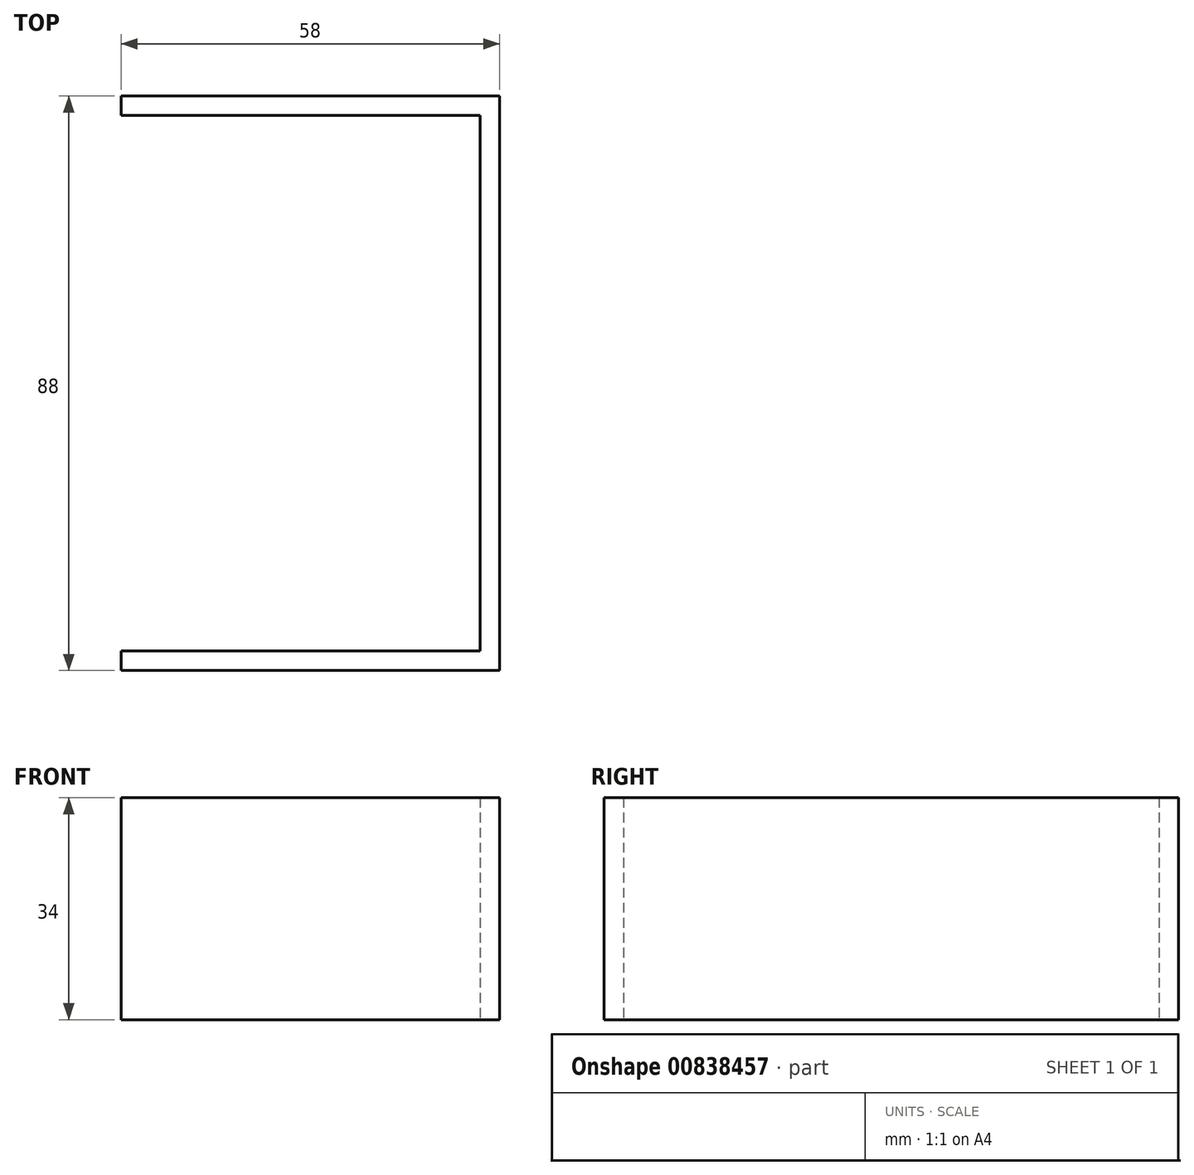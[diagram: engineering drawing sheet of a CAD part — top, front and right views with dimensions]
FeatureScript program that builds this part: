
annotation { "Feature Type Name" : "Feature", "Feature Type Description" : "" }
export const myFeature = defineFeature(function(context is Context, id is Id, definition is map)
    precondition{}
    {
        {
            var Q0;
            Q0=qCreatedBy(makeId("Top.planeOp"),FACE);
            var sketch = newSketch(context, id + "F0", { "sketchPlane" : qUnion([Q0])});
            skLineSegment(sketch, "E0", {"start": v(-18.99, 72.27) * mm, "end": v(39.01, 72.27) * mm});
            skLineSegment(sketch, "E1", {"start": v(39.01, 72.27) * mm, "end": v(39.01, -15.73) * mm});
            skLineSegment(sketch, "E2", {"start": v(39.01, -15.73) * mm, "end": v(-18.99, -15.73) * mm});
            skLineSegment(sketch, "E3", {"start": v(-18.99, -15.73) * mm, "end": v(-18.99, -12.73) * mm});
            skLineSegment(sketch, "E4", {"start": v(-18.99, -12.73) * mm, "end": v(36.01, -12.73) * mm});
            skLineSegment(sketch, "E5", {"start": v(36.01, -12.73) * mm, "end": v(36.01, 69.27) * mm});
            skLineSegment(sketch, "E6", {"start": v(36.01, 69.27) * mm, "end": v(-18.99, 69.27) * mm});
            skLineSegment(sketch, "E7", {"start": v(-18.99, 69.27) * mm, "end": v(-18.99, 72.27) * mm});
            skSolve(sketch);
        }
        {
            var Q0;
            Q0=makeQuery(id+"F0.imprint","IMPRINT",FACE,{"disambiguationData":[TD([[makeQuery(id+"F0.imprint","IMPRINT",EDGE,{"derivedFrom":sQuery(id+"F0.wireOp",EDGE,"E0")}),-1.0]])]});
            extrude(context, id + "F1", {"entities" : qUnion([Q0]), "depth" : 34 * mm, "offsetDistance" : 25 * mm});
        }
    });
